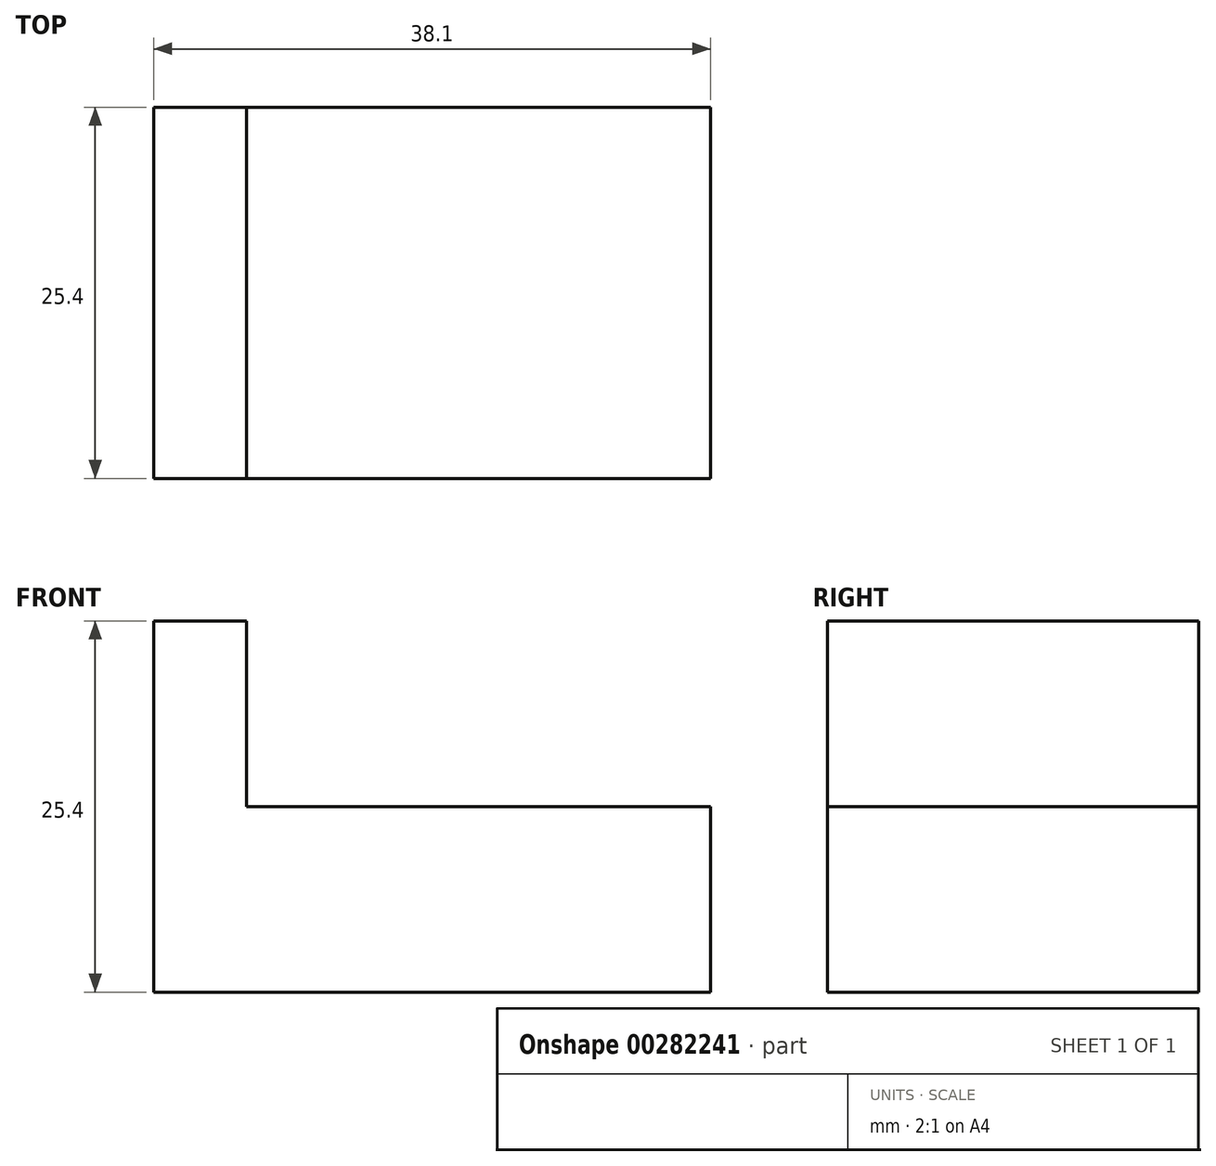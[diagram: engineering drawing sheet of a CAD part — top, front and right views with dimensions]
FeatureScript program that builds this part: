
annotation { "Feature Type Name" : "Feature", "Feature Type Description" : "" }
export const myFeature = defineFeature(function(context is Context, id is Id, definition is map)
    precondition{}
    {
        {
            var Q0;
            Q0=qCreatedBy(makeId("Front.planeOp"),FACE);
            var sketch = newSketch(context, id + "F0", { "sketchPlane" : qUnion([Q0])});
            skLineSegment(sketch, "E0", {"start": v(0, 0) * mm, "end": v(0, 25.4) * mm});
            skLineSegment(sketch, "E1", {"start": v(0, 25.4) * mm, "end": v(6.35, 25.4) * mm});
            skLineSegment(sketch, "E2", {"start": v(6.35, 25.4) * mm, "end": v(6.35, 12.7) * mm});
            skLineSegment(sketch, "E3", {"start": v(6.35, 12.7) * mm, "end": v(38.1, 12.7) * mm});
            skLineSegment(sketch, "E4", {"start": v(38.1, 12.7) * mm, "end": v(38.1, 0) * mm});
            skLineSegment(sketch, "E5", {"start": v(38.1, 0) * mm, "end": v(0, 0) * mm});
            skSolve(sketch);
        }
        {
            var Q0;
            Q0=makeQuery(id+"F0.imprint","IMPRINT",FACE,{"disambiguationData":[TD([[makeQuery(id+"F0.imprint","IMPRINT",EDGE,{"derivedFrom":sQuery(id+"F0.wireOp",EDGE,"E0")}),-1.0]])]});
            extrude(context, id + "F1", {"entities" : qUnion([Q0]), "endBound" : BoundingType.SYMMETRIC, "depth" : 25.4 * mm});
        }
    });
